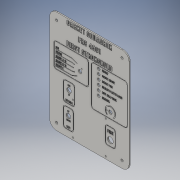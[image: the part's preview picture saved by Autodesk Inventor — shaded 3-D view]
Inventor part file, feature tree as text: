
AUTODESK INVENTOR PART (.ipt)
format: ipt  version: 2016 (Build 200138000, 138)  size: 2,188,288 bytes
history: native  units: in
note: dims shown in document units (in); Inventor stores cm internally (conversion verified against a paired STEP export)
features: emboss x19, projected_geometry x7, other x2, extrude x2, plane x1
ambient origin geometry x8: Origin, YZ Plane, XZ Plane, XY Plane, X Axis, Y Axis, Z Axis, Center Point
bodies: Body1 (feature_tree)
feature tree (31):
  other  "Cut"
  plane  "Work Plane2"
  extrude  "Extrusion3"  Depth=11.0in
  extrude  "Extrusion5"  Depth=0.25in
  emboss  "Emboss2"
  emboss  "Emboss3"
  emboss  "Emboss4"
  emboss  "Emboss5"
  emboss  "Emboss6"
  emboss  "Emboss7"
  emboss  "Emboss8"
  emboss  "Emboss9"
  emboss  "Emboss10"
  emboss  "Emboss11"
  emboss  "Emboss12"
  emboss  "Emboss13"
  emboss  "Emboss14"
  emboss  "Emboss15"
  emboss  "Emboss16"
  emboss  "Emboss17"
  emboss  "Emboss18"
  emboss  "Emboss19"
  emboss  "Emboss20"
  other  "Etch"
  projected_geometry  "Projected Loop5"
  projected_geometry  "Projected Loop8"
  projected_geometry  "Projected Loop9"
  projected_geometry  "Projected Loop10"
  projected_geometry  "Projected Loop11"
  projected_geometry  "Projected Loop12"
  projected_geometry  "Projected Loop13"
